# Revit family: KDW010014
name_source: partatom
category: Plumbing Fixtures
revit_build: Autodesk Revit 2015 (Build: 20140606_1530(x64)
units: mm (PartAtom-declared; Revit-internal decimal feet)

## types (1)
- KDW010014
    BIMobject category = Bath & Spas
    Brand url = http://www.kaldewei.com
    Color = https://www.kaldewei.co.uk
    ColourOptions = https://www.kaldewei.co.uk
    ConnectingDimensions = EN 232
    Design country = Germany
    DrainSize = 52 mm
    Durability = https://www.kaldewei.de
    Edition number = 1
    Features = https://www.kaldewei.co.uk
    Finish = https://www.kaldewei.co.uk
    Finition = Kaldewei
    HasGrabHandles = https://www.kaldewei.co.uk
    IFC Classification = Furnishing Element
    IfcExportAs = BATH
    IfcExportType = IfcSanitaryTerminalType
    IntegralAccessories = https://www.kaldewei.co.uk
    Manufacturer = Kaldewei
    Manufacturer country = Germany
    ManufacturerCountry = GERMANY
    ManufacturerName = KALDEWEI
    ManufacturerURL = https://www.kaldewei.com
    Material = steel enamel
    Material main = Steel
    Material secondary = Enamel
    Model = CENTRO DUO 1 RECHTS
    NBS Reference Code = 35-06-08
    NBS Reference Description = Baths
    Name = CENTRO DUO 1 right
    Nominal height = 750 cm
    Nominal width = 1700 cm
    NominalDepth = 485
    NominalLength = 1700
    ObjectName = CENTRO DUO 1 right 750x1700x485
    ObjectNorm = EN 14516EU DECLARATION OF PERFORMANCE(https://www.kaldewei.de
    ObjectPicture = https://www.kaldewei.co.uk
    ObjectURL = https://www.kaldewei.co.uk
    Polantis code = KDW010014
    Product Guid = 34578a9c-86e6-4e1e-a3f2-cdfc84a2d159
    Product SKU = 130
    Product certification = https://www.kaldewei.co.uk
    Product data url = http://bimobject.com
    Product family = CENTRO DUO
    Product group = Bathtub
    Product url = https://www.kaldewei.co.uk
    ProductInformation = Model No.130: Pure and elegant.The basic oval shape, the extra depth of 47 cm as well as identical backrests and centrally placed waste, it’s also the right bath for two to enjoy comfortably.
    QR code = http://bimobject.com
    Revision = 1
    SerialNumber = 130
    Shape = Special shapes
    Size = 750x1700x485
    SupportFrame = https://www.kaldewei.co.uk
    Sustainability = https://kaldewei-fa.secure.footprint.net
    Technical description = https://www.kaldewei.co.uk
    TechnicalDataURL = https://kaldewei.typo-live.web-factory.de
    Type Comments = CENTRO DUO 1 LINKS CENTRO DUO 1 RECHTS 130 750x1700x485
    UNSPSC Code = 30181501
    UNSPSCCode = 30181500
    UNSPSCNames = Sanitary ware
    URL = https://www.kaldewei.co.uk
    Uniclass 1.4 Code = L7211
    Uniclass 1.4 Description = Baths
    Uniclass 2.0 Code = PR-35-06-08
    Uniclass 2.0 Description = Baths
    Uniclass 2015 = Pr_40_20_06_08
    Version = 4
    VolumeToOverflowMaximum = 156
    WarrantyDurationParts = 30
    WarrantyDurationUnit = Year
    WarrantyStartDate = https://www.kaldewei.co.uk
    WaterSupplyOverflowAndWasteHolesOverflow = 52 mm
    WaterSupplyOverflowAndWasteHolesWaste = 52 mm
    Weight = 53
    Weight Net (Kg) = 53

## geometry (parser evidence)
native form markers: Sweep x2
no freeform markers — native parametric forms only
